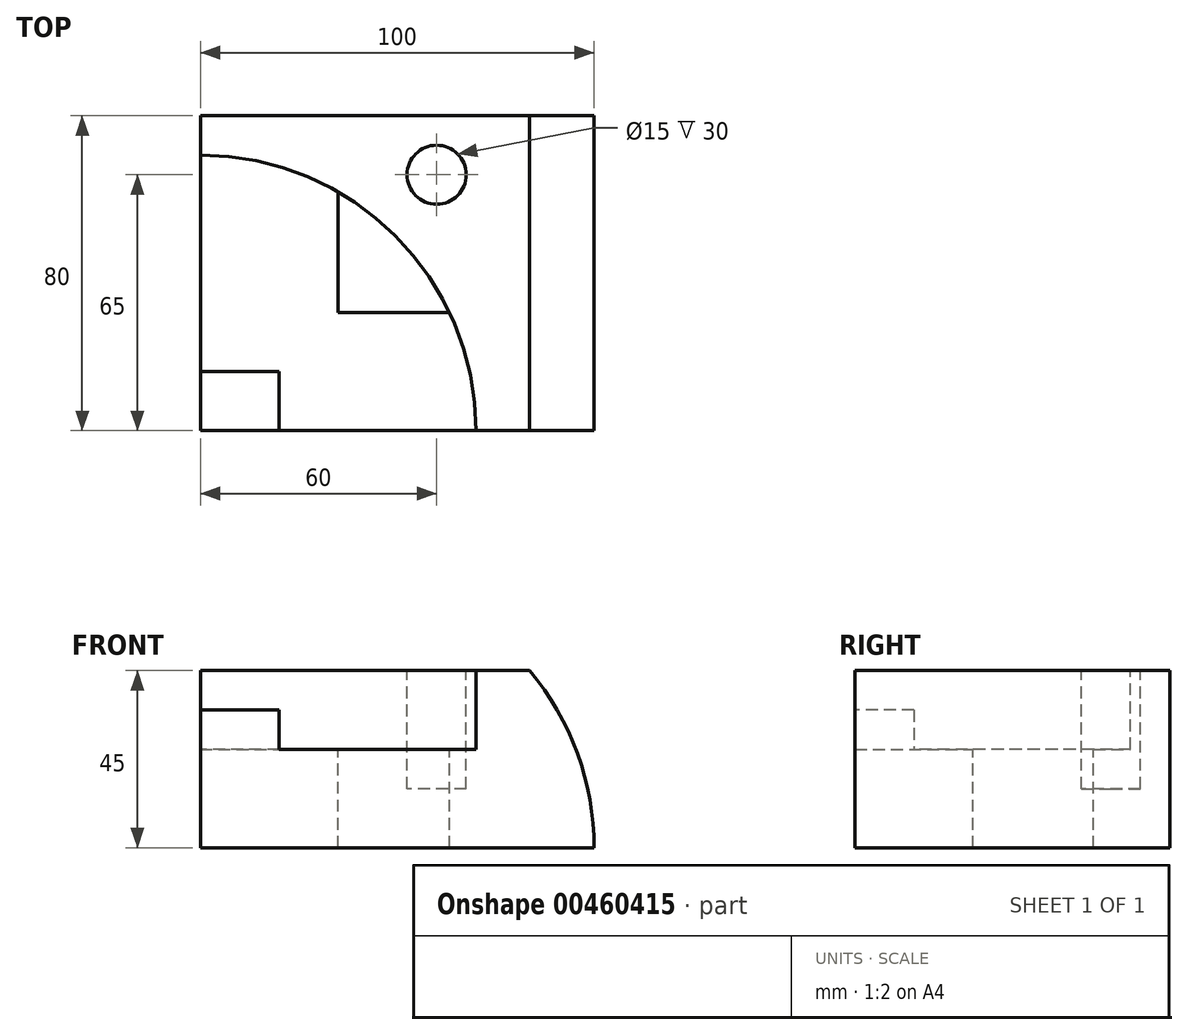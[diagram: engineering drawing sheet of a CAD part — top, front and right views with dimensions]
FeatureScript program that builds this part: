
annotation { "Feature Type Name" : "Feature", "Feature Type Description" : "" }
export const myFeature = defineFeature(function(context is Context, id is Id, definition is map)
    precondition{}
    {
        {
            var Q0;
            Q0=qCreatedBy(makeId("Top.planeOp"),FACE);
            var sketch = newSketch(context, id + "F0", { "sketchPlane" : qUnion([Q0])});
            skLineSegment(sketch, "E0.bottom", {"start": v(0, 0) * mm, "end": v(100, 0) * mm});
            skLineSegment(sketch, "E0.top", {"start": v(0, -80) * mm, "end": v(100, -80) * mm});
            skLineSegment(sketch, "E0.left", {"start": v(0, 0) * mm, "end": v(0, -80) * mm});
            skLineSegment(sketch, "E0.right", {"start": v(100, 0) * mm, "end": v(100, -80) * mm});
            skSolve(sketch);
        }
        {
            var Q0;
            Q0 = qSketchRegion(id + "F0", true);
            extrude(context, id + "F1", {"entities" : qUnion([Q0]), "depth" : 45 * mm});
        }
        {
            var Q0;
            Q0=makeQuery(id+"F1.opExtrude","CAP_FACE",FACE,{"disambiguationData":[OSD([sQuery(id+"F0.wireOp",EDGE,"E0.bottom"),sQuery(id+"F0.wireOp",EDGE,"E0.top"),sQuery(id+"F0.wireOp",EDGE,"E0.left"),sQuery(id+"F0.wireOp",EDGE,"E0.right")])],"isStart":false});
            var sketch = newSketch(context, id + "F2", { "sketchPlane" : qUnion([Q0])});
            skCircle(sketch, "E1", {"center": v(0, -80) * mm, "radius": 70 * mm});
            skSolve(sketch);
        }
        {
            var Q0;
            Q0 = qSketchRegion(id + "F2", true);
            extrude(context, id + "F3", {"entities" : qUnion([Q0]), "operationType" : NewBodyOperationType.REMOVE, "oppositeDirection" : true, "depth" : 20 * mm});
        }
        {
            var Q0;
            Q0=makeQuery(id+"F3.boolean.opBoolean","COPY",FACE,{"derivedFrom":makeQuery(id+"F3.opExtrude","CAP_FACE",FACE,{"disambiguationData":[OSD([sQuery(id+"F2.wireOp",EDGE,"E1")])],"isStart":false})});
            var sketch = newSketch(context, id + "F4", { "sketchPlane" : qUnion([Q0])});
            skLineSegment(sketch, "E2.bottom", {"start": v(0, -80) * mm, "end": v(20, -80) * mm});
            skLineSegment(sketch, "E2.top", {"start": v(0, -65) * mm, "end": v(20, -65) * mm});
            skLineSegment(sketch, "E2.left", {"start": v(0, -80) * mm, "end": v(0, -65) * mm});
            skLineSegment(sketch, "E2.right", {"start": v(20, -80) * mm, "end": v(20, -65) * mm});
            skSolve(sketch);
        }
        {
            var Q0;
            Q0=makeQuery(id+"F4.imprint","IMPRINT",FACE,{"disambiguationData":[TD([[makeQuery(id+"F4.imprint","IMPRINT",EDGE,{"derivedFrom":sQuery(id+"F4.wireOp",EDGE,"E2.bottom")}),1.0]])]});
            extrude(context, id + "F5", {"entities" : qUnion([Q0]), "operationType" : NewBodyOperationType.ADD, "depth" : 10 * mm});
        }
        {
            var Q0;
            Q0=makeQuery(id+"F3.boolean.opBoolean","COPY",FACE,{"derivedFrom":makeQuery(id+"F3.opExtrude","CAP_FACE",FACE,{"disambiguationData":[OSD([sQuery(id+"F2.wireOp",EDGE,"E1")])],"isStart":false})});
            var sketch = newSketch(context, id + "F6", { "sketchPlane" : qUnion([Q0])});
            skArc(sketch, "E3", {"start": v(63.25, -50) * mm, "mid": v(51.45, -32.54) * mm, "end": v(35, -19.38) * mm});
            skLineSegment(sketch, "E4", {"start": v(35, -19.38) * mm, "end": v(35, -50) * mm});
            skLineSegment(sketch, "E5", {"start": v(35, -50) * mm, "end": v(63.25, -50) * mm});
            skSolve(sketch);
        }
        {
            var Q0;
            Q0 = qSketchRegion(id + "F6", true);
            extrude(context, id + "F7", {"entities" : qUnion([Q0]), "operationType" : NewBodyOperationType.REMOVE, "oppositeDirection" : true, "depth" : 151.8 * mm});
        }
        {
            var Q0;
            Q0=makeQuery(id+"F1.opExtrude","CAP_FACE",FACE,{"disambiguationData":[OSD([sQuery(id+"F0.wireOp",EDGE,"E0.bottom"),sQuery(id+"F0.wireOp",EDGE,"E0.top"),sQuery(id+"F0.wireOp",EDGE,"E0.left"),sQuery(id+"F0.wireOp",EDGE,"E0.right")])],"isStart":false});
            var sketch = newSketch(context, id + "F8", { "sketchPlane" : qUnion([Q0])});
            skCircle(sketch, "E6", {"center": v(60, -15) * mm, "radius": 7.5 * mm});
            skSolve(sketch);
        }
        {
            var Q0;
            Q0 = qSketchRegion(id + "F8", true);
            extrude(context, id + "F9", {"entities" : qUnion([Q0]), "operationType" : NewBodyOperationType.REMOVE, "oppositeDirection" : true, "depth" : 30 * mm});
        }
        {
            var Q0;
            Q0=makeQuery(id+"F5.boolean.opBoolean","MERGE",FACE,{"derivedFrom":[makeQuery(id+"F1.opExtrude","SWEPT_FACE",FACE,{"disambiguationData":[OSD([sQuery(id+"F0.wireOp",EDGE,"E0.top")])]}),makeQuery(id+"F5.opExtrude","SWEPT_FACE",FACE,{"disambiguationData":[OSD([sQuery(id+"F4.wireOp",EDGE,"E2.bottom")])]})]});
            var sketch = newSketch(context, id + "F10", { "sketchPlane" : qUnion([Q0])});
            skArc(sketch, "E7", {"start": v(100, 0) * mm, "mid": v(95.78, 23.94) * mm, "end": v(83.62, 45) * mm});
            skSolve(sketch);
        }
        {
            var Q0;
            Q0 = qSketchRegion(id + "F10", true);
            var Q1;
            {var subQ0=sQuery(id+"F10.wireOp",EDGE,"E7");Q1=makeQuery(id+"F10.imprint","IMPRINT",FACE,{"disambiguationData":[TD([[makeQuery(id+"F10.imprint","IMPRINT",EDGE,{"derivedFrom":subQ0}),-1.0]])]});}
            extrude(context, id + "F11", {"entities" : qUnion([Q0, Q1]), "operationType" : NewBodyOperationType.REMOVE, "oppositeDirection" : true, "depth" : 85.3 * mm});
        }
    });
